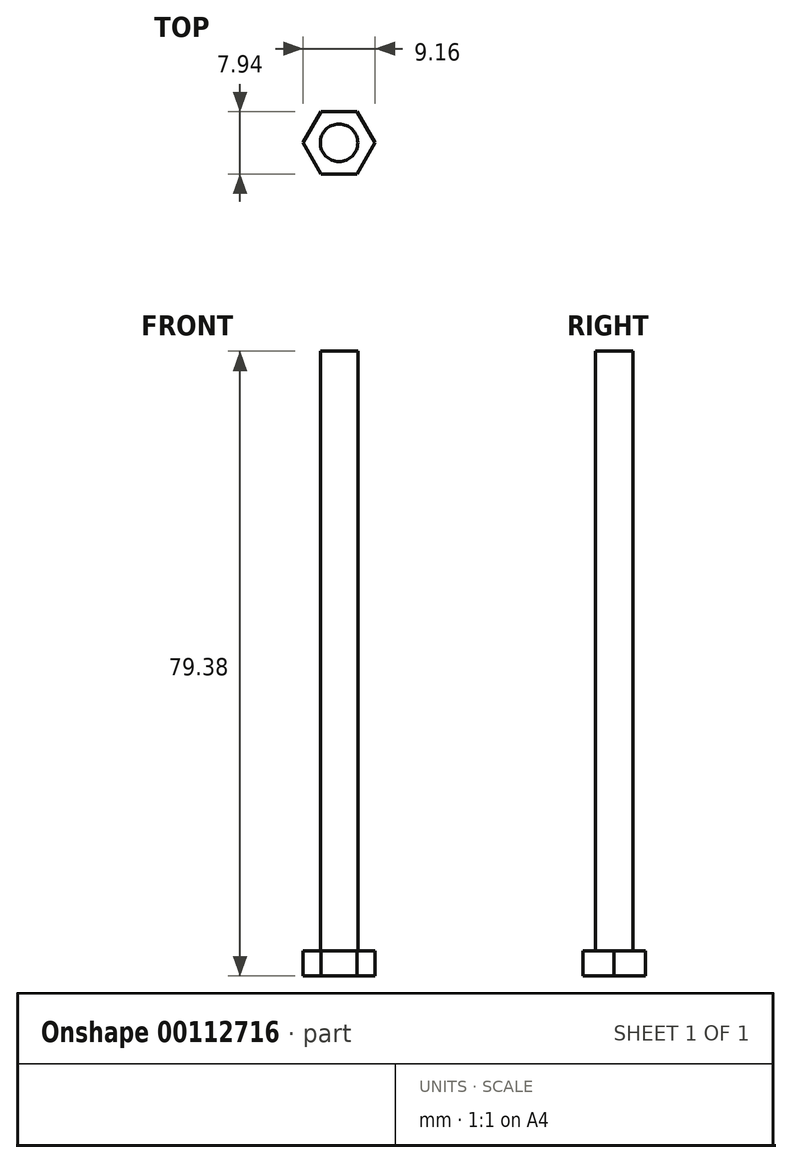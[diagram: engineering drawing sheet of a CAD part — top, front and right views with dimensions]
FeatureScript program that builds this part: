
annotation { "Feature Type Name" : "Feature", "Feature Type Description" : "" }
export const myFeature = defineFeature(function(context is Context, id is Id, definition is map)
    precondition{}
    {
        {
            var Q0;
            Q0=qCreatedBy(makeId("Top.planeOp"),FACE);
            var sketch = newSketch(context, id + "F0", { "sketchPlane" : qUnion([Q0])});
            skCircle(sketch, "E0.cCircle", {"center": v(0, 0) * mm, "radius": 3.97 * mm, "construction": true});
            skLineSegment(sketch, "E0.0", {"start": v(2.3, -3.97) * mm, "end": v(-2.3, -3.97) * mm});
            skLineSegment(sketch, "E0.1", {"start": v(-2.3, -3.97) * mm, "end": v(-4.58, 0) * mm});
            skLineSegment(sketch, "E0.2", {"start": v(-4.58, 0) * mm, "end": v(-2.3, 3.97) * mm});
            skLineSegment(sketch, "E0.3", {"start": v(-2.3, 3.97) * mm, "end": v(2.3, 3.97) * mm});
            skLineSegment(sketch, "E0.4", {"start": v(2.3, 3.97) * mm, "end": v(4.58, 0) * mm});
            skLineSegment(sketch, "E0.5", {"start": v(4.58, 0) * mm, "end": v(2.3, -3.97) * mm});
            skPoint(sketch, "E0.0.midPoint", {"position": v(0, -3.97) * mm});
            skSolve(sketch);
        }
        {
            var Q0;
            Q0 = qSketchRegion(id + "F0", true);
            extrude(context, id + "F1", {"entities" : qUnion([Q0]), "depth" : 3.17 * mm});
        }
        {
            var Q0;
            Q0=makeQuery(id+"F1.opExtrude","CAP_FACE",FACE,{"disambiguationData":[OSD([sQuery(id+"F0.wireOp",EDGE,"E0.0"),sQuery(id+"F0.wireOp",EDGE,"E0.1"),sQuery(id+"F0.wireOp",EDGE,"E0.2"),sQuery(id+"F0.wireOp",EDGE,"E0.3"),sQuery(id+"F0.wireOp",EDGE,"E0.4"),sQuery(id+"F0.wireOp",EDGE,"E0.5")])],"isStart":false});
            var sketch = newSketch(context, id + "F2", { "sketchPlane" : qUnion([Q0])});
            skCircle(sketch, "E1", {"center": v(0, 0) * mm, "radius": 2.38 * mm});
            skSolve(sketch);
        }
        {
            var Q0;
            Q0 = qSketchRegion(id + "F2", true);
            extrude(context, id + "F3", {"entities" : qUnion([Q0]), "operationType" : NewBodyOperationType.ADD, "depth" : 76.2 * mm});
        }
    });
